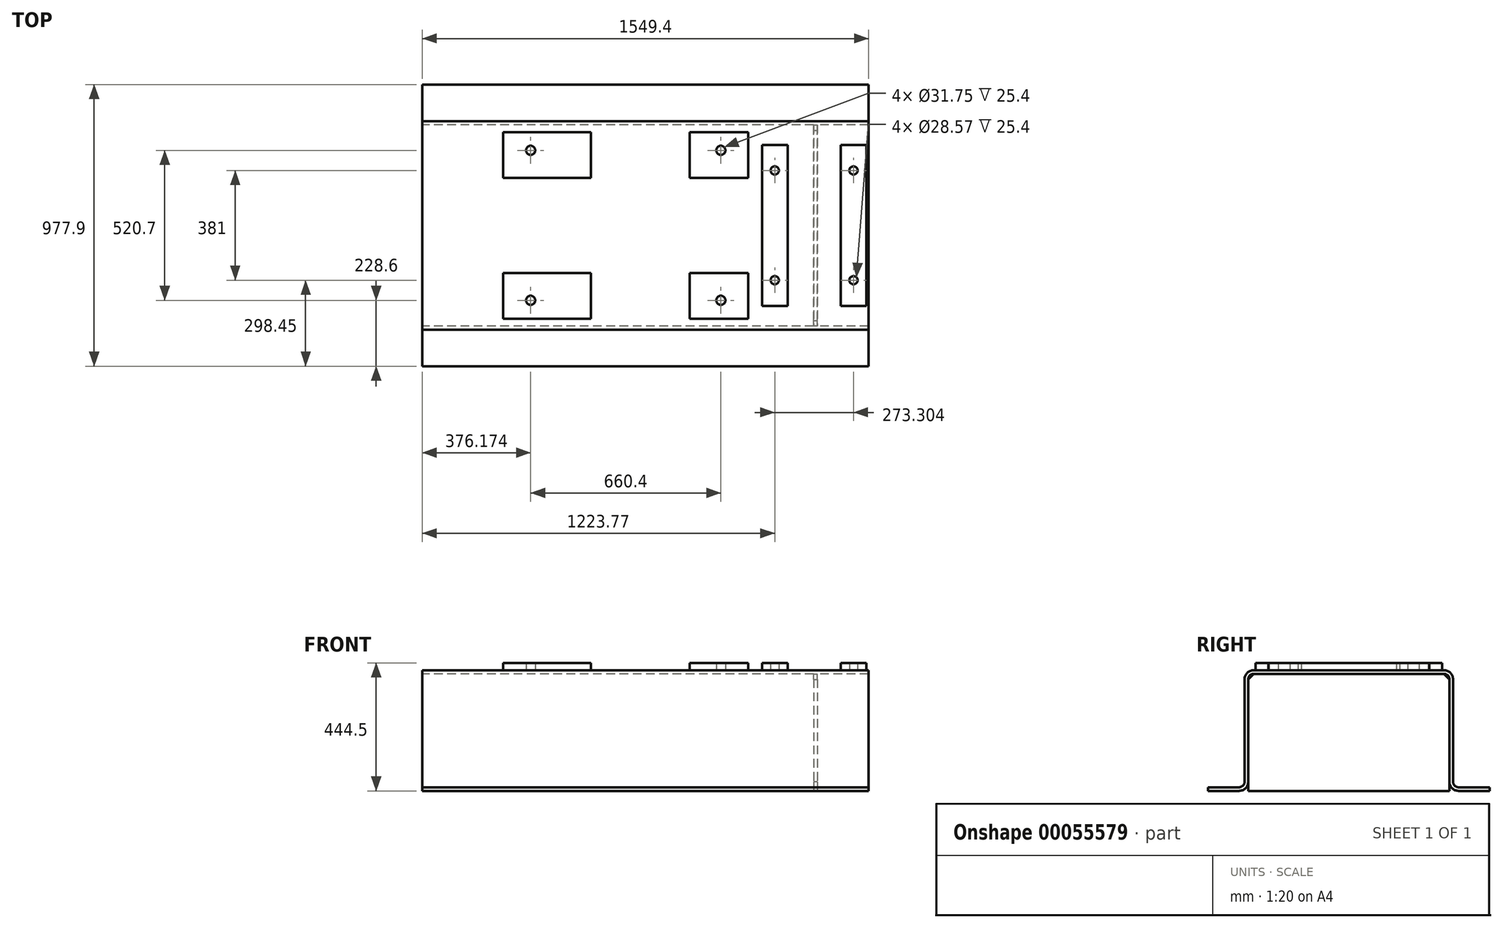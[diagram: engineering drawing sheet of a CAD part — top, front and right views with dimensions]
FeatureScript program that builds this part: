
annotation { "Feature Type Name" : "Feature", "Feature Type Description" : "" }
export const myFeature = defineFeature(function(context is Context, id is Id, definition is map)
    precondition{}
    {
        {
            var Q0;
            Q0=qCreatedBy(makeId("Right.planeOp"),FACE);
            var sketch = newSketch(context, id + "F0", { "sketchPlane" : qUnion([Q0])});
            skLineSegment(sketch, "E0.rect.bottom", {"start": v(-330.2, 209.55) * mm, "end": v(0, 209.55) * mm});
            skLineSegment(sketch, "E0.rect.top", {"start": v(-488.95, -209.55) * mm, "end": v(-381, -209.55) * mm});
            skLineSegment(sketch, "E0.rect.right", {"start": v(488.95, 209.55) * mm, "end": v(488.95, -209.55) * mm, "construction": true});
            skPoint(sketch, "E0.rect.middle", {"position": v(0, 0) * mm});
            skLineSegment(sketch, "E1", {"start": v(0, -296.04) * mm, "end": v(0, 331.56) * mm, "construction": true});
            skPoint(sketch, "E1.endSnap0", {"position": v(0, 209.55) * mm});
            skLineSegment(sketch, "E2.0", {"start": v(-361.95, 177.8) * mm, "end": v(-361.95, -177.8) * mm});
            skLineSegment(sketch, "E3.0", {"start": v(-349.25, 177.8) * mm, "end": v(-349.25, -177.8) * mm});
            skLineSegment(sketch, "E4.0", {"start": v(-488.95, -196.85) * mm, "end": v(-381, -196.85) * mm});
            skLineSegment(sketch, "E5.0", {"start": v(-330.2, 196.85) * mm, "end": v(0, 196.85) * mm});
            skLineSegment(sketch, "E6.trimOffspring", {"start": v(0, -196.85) * mm, "end": v(488.95, -196.85) * mm, "construction": true});
            skLineSegment(sketch, "E7.trimOffspring", {"start": v(0, -209.55) * mm, "end": v(488.95, -209.55) * mm, "construction": true});
            skLineSegment(sketch, "E8.trimOffspring", {"start": v(-488.95, -196.85) * mm, "end": v(-488.95, -209.55) * mm});
            skPoint(sketch, "E0.rect.left.start.orphan", {"position": v(-488.95, 209.55) * mm});
            skPoint(sketch, "E9.visualSharp", {"position": v(-349.25, 196.85) * mm});
            skArc(sketch, "E9.filletArc", {"start": v(-330.2, 196.85) * mm, "mid": v(-343.67, 191.27) * mm, "end": v(-349.25, 177.8) * mm});
            skPoint(sketch, "E10.visualSharp", {"position": v(-361.95, -196.85) * mm});
            skArc(sketch, "E10.filletArc", {"start": v(-381, -196.85) * mm, "mid": v(-367.53, -191.27) * mm, "end": v(-361.95, -177.8) * mm});
            skPoint(sketch, "E11.visualSharp", {"position": v(-349.25, -209.55) * mm});
            skArc(sketch, "E11.filletArc", {"start": v(-381, -209.55) * mm, "mid": v(-358.55, -200.25) * mm, "end": v(-349.25, -177.8) * mm});
            skPoint(sketch, "E12.visualSharp", {"position": v(-361.95, 209.55) * mm});
            skArc(sketch, "E12.filletArc", {"start": v(-330.2, 209.55) * mm, "mid": v(-352.65, 200.25) * mm, "end": v(-361.95, 177.8) * mm});
            skArc(sketch, "E13.MirrorCS", {"start": v(381, -196.85) * mm, "mid": v(367.53, -191.27) * mm, "end": v(361.95, -177.8) * mm});
            skArc(sketch, "E14.MirrorCS", {"start": v(330.2, 196.85) * mm, "mid": v(343.67, 191.27) * mm, "end": v(349.25, 177.8) * mm});
            skLineSegment(sketch, "E15.MirrorCS", {"start": v(488.95, -196.85) * mm, "end": v(488.95, -209.55) * mm});
            skArc(sketch, "E16.MirrorCS", {"start": v(330.2, 209.55) * mm, "mid": v(352.65, 200.25) * mm, "end": v(361.95, 177.8) * mm});
            skArc(sketch, "E17.MirrorCS", {"start": v(381, -209.55) * mm, "mid": v(358.55, -200.25) * mm, "end": v(349.25, -177.8) * mm});
            skLineSegment(sketch, "E18.MirrorCS", {"start": v(330.2, 209.55) * mm, "end": v(0, 209.55) * mm});
            skPoint(sketch, "E19.MirrorP", {"position": v(349.25, -209.55) * mm});
            skLineSegment(sketch, "E20.MirrorCS", {"start": v(488.95, -209.55) * mm, "end": v(381, -209.55) * mm});
            skPoint(sketch, "E21.MirrorP", {"position": v(361.95, 209.55) * mm});
            skLineSegment(sketch, "E22.MirrorCS", {"start": v(330.2, 196.85) * mm, "end": v(0, 196.85) * mm});
            skLineSegment(sketch, "E23.MirrorCS", {"start": v(488.95, -196.85) * mm, "end": v(381, -196.85) * mm});
            skPoint(sketch, "E24.MirrorP", {"position": v(488.95, 209.55) * mm});
            skPoint(sketch, "E25.MirrorP", {"position": v(361.95, -196.85) * mm});
            skLineSegment(sketch, "E26.MirrorCS", {"start": v(361.95, 177.8) * mm, "end": v(361.95, -177.8) * mm});
            skLineSegment(sketch, "E27.MirrorCS", {"start": v(349.25, 177.8) * mm, "end": v(349.25, -177.8) * mm});
            skPoint(sketch, "E28.MirrorP", {"position": v(349.25, 196.85) * mm});
            skSolve(sketch);
        }
        {
            var Q0;
            Q0=makeQuery(id+"F0.imprint","IMPRINT",FACE,{"disambiguationData":[TD([[makeQuery(id+"F0.imprint","IMPRINT",EDGE,{"derivedFrom":sQuery(id+"F0.wireOp",EDGE,"E0.rect.bottom")}),-1.0]])]});
            extrude(context, id + "F1", {"entities" : qUnion([Q0]), "endBound" : BoundingType.SYMMETRIC, "depth" : 1549.4 * mm});
        }
        {
            var Q0;
            Q0=makeQuery(id+"F1.opExtrude","SWEPT_FACE",FACE,{"disambiguationData":[OSD([sQuery(id+"F0.wireOp",EDGE,"E0.rect.bottom"),sQuery(id+"F0.wireOp",EDGE,"E18.MirrorCS")])]});
            var sketch = newSketch(context, id + "F2", { "sketchPlane" : qUnion([Q0])});
            skLineSegment(sketch, "E29.0", {"start": v(-774.7, -330.2) * mm, "end": v(-774.7, 330.2) * mm, "construction": true});
            skLineSegment(sketch, "E30.0", {"start": v(-68.33, -330.2) * mm, "end": v(-68.33, 330.2) * mm, "construction": true});
            skLineSegment(sketch, "E31.0", {"start": v(585.72, -330.2) * mm, "end": v(585.72, 330.2) * mm, "construction": true});
            skLineSegment(sketch, "E32", {"start": v(-867.52, 0) * mm, "end": v(843.8, 0) * mm, "construction": true});
            skPoint(sketch, "E32.startSnap0", {"position": v(-774.7, 0) * mm});
            skLineSegment(sketch, "E33.0", {"start": v(153.92, -330.2) * mm, "end": v(153.92, 330.2) * mm, "construction": true});
            skLineSegment(sketch, "E34.0", {"start": v(357.12, -330.2) * mm, "end": v(357.12, 330.2) * mm, "construction": true});
            skLineSegment(sketch, "E35.0", {"start": v(-188.98, -330.2) * mm, "end": v(-188.98, 330.2) * mm, "construction": true});
            skLineSegment(sketch, "E36.0", {"start": v(-493.78, -330.2) * mm, "end": v(-493.78, 330.2) * mm, "construction": true});
            skLineSegment(sketch, "E37.0", {"start": v(-867.52, -165.1) * mm, "end": v(843.8, -165.1) * mm, "construction": true});
            skLineSegment(sketch, "E38.0", {"start": v(-867.52, -323.85) * mm, "end": v(843.8, -323.85) * mm, "construction": true});
            skLineSegment(sketch, "E39.bottom", {"start": v(-188.98, -323.85) * mm, "end": v(-493.78, -323.85) * mm});
            skLineSegment(sketch, "E39.top", {"start": v(-188.98, -165.1) * mm, "end": v(-493.78, -165.1) * mm});
            skLineSegment(sketch, "E39.left", {"start": v(-188.98, -323.85) * mm, "end": v(-188.98, -165.1) * mm});
            skLineSegment(sketch, "E39.right", {"start": v(-493.78, -323.85) * mm, "end": v(-493.78, -165.1) * mm});
            skLineSegment(sketch, "E40.bottom", {"start": v(153.92, -165.1) * mm, "end": v(357.12, -165.1) * mm});
            skLineSegment(sketch, "E40.top", {"start": v(153.92, -323.85) * mm, "end": v(357.12, -323.85) * mm});
            skLineSegment(sketch, "E40.left", {"start": v(153.92, -165.1) * mm, "end": v(153.92, -323.85) * mm});
            skLineSegment(sketch, "E40.right", {"start": v(357.12, -165.1) * mm, "end": v(357.12, -323.85) * mm});
            skLineSegment(sketch, "E41.0", {"start": v(-398.53, -330.2) * mm, "end": v(-398.53, 330.2) * mm, "construction": true});
            skLineSegment(sketch, "E42.0", {"start": v(-867.52, -260.35) * mm, "end": v(843.8, -260.35) * mm, "construction": true});
            skCircle(sketch, "E43", {"center": v(-398.53, -260.35) * mm, "radius": 15.88 * mm});
            skCircle(sketch, "E44.MirrorC", {"center": v(261.87, -260.35) * mm, "radius": 15.88 * mm});
            skCircle(sketch, "E45.MirrorC", {"center": v(-398.53, 260.35) * mm, "radius": 15.88 * mm});
            skCircle(sketch, "E46.MirrorC", {"center": v(261.87, 260.35) * mm, "radius": 15.88 * mm});
            skLineSegment(sketch, "E47.MirrorCS", {"start": v(153.92, 323.85) * mm, "end": v(357.12, 323.85) * mm});
            skLineSegment(sketch, "E48.MirrorCS", {"start": v(-188.98, 323.85) * mm, "end": v(-493.78, 323.85) * mm});
            skLineSegment(sketch, "E49.MirrorCS", {"start": v(-188.98, 165.1) * mm, "end": v(-493.78, 165.1) * mm});
            skLineSegment(sketch, "E50.MirrorCS", {"start": v(-188.98, 323.85) * mm, "end": v(-188.98, 165.1) * mm});
            skLineSegment(sketch, "E51.MirrorCS", {"start": v(153.92, 165.1) * mm, "end": v(153.92, 323.85) * mm});
            skLineSegment(sketch, "E52.MirrorCS", {"start": v(357.12, 165.1) * mm, "end": v(357.12, 323.85) * mm});
            skLineSegment(sketch, "E53.MirrorCS", {"start": v(153.92, 165.1) * mm, "end": v(357.12, 165.1) * mm});
            skLineSegment(sketch, "E54.MirrorCS", {"start": v(-493.78, 323.85) * mm, "end": v(-493.78, 165.1) * mm});
            skLineSegment(sketch, "E55.0", {"start": v(493.78, -330.2) * mm, "end": v(493.78, -323.85) * mm});
            skLineSegment(sketch, "E56.0", {"start": v(404.88, -330.2) * mm, "end": v(404.88, -323.85) * mm});
            skLineSegment(sketch, "E57.trimOffspring", {"start": v(404.88, 279.4) * mm, "end": v(493.78, 279.4) * mm});
            skLineSegment(sketch, "E58.trimOffspring", {"start": v(493.78, -279.4) * mm, "end": v(493.78, 279.4) * mm});
            skLineSegment(sketch, "E59.trimOffspring", {"start": v(404.88, -279.4) * mm, "end": v(404.88, 279.4) * mm});
            skLineSegment(sketch, "E60.trimOffspring", {"start": v(404.88, -279.4) * mm, "end": v(493.78, -279.4) * mm});
            skLineSegment(sketch, "E61.0", {"start": v(449.07, -330.2) * mm, "end": v(449.07, 330.2) * mm, "construction": true});
            skLineSegment(sketch, "E62.0", {"start": v(-867.52, 190.5) * mm, "end": v(843.8, 190.5) * mm, "construction": true});
            skCircle(sketch, "E63", {"center": v(449.07, 190.5) * mm, "radius": 14.29 * mm});
            skCircle(sketch, "E64.MirrorC", {"center": v(449.07, -190.5) * mm, "radius": 14.29 * mm});
            skCircle(sketch, "E65.MirrorC", {"center": v(722.38, -190.5) * mm, "radius": 14.29 * mm});
            skCircle(sketch, "E66.MirrorC", {"center": v(722.38, 190.5) * mm, "radius": 14.29 * mm});
            skLineSegment(sketch, "E67.MirrorCS", {"start": v(766.57, -279.4) * mm, "end": v(766.57, 279.4) * mm});
            skLineSegment(sketch, "E68.MirrorCS", {"start": v(677.67, -279.4) * mm, "end": v(677.67, 279.4) * mm});
            skLineSegment(sketch, "E69.MirrorCS", {"start": v(766.57, 279.4) * mm, "end": v(677.67, 279.4) * mm});
            skLineSegment(sketch, "E70.MirrorCS", {"start": v(766.57, -279.4) * mm, "end": v(677.67, -279.4) * mm});
            skSolve(sketch);
        }
        {
            var Q0;
            Q0=qSketchRegion(id+"F2",true);
            extrude(context, id + "F3", {"entities" : qUnion([Q0]), "operationType" : NewBodyOperationType.ADD, "depth" : 25.4 * mm});
        }
        {
            var Q0;
            Q0=makeQuery(id+"F1.opExtrude","CAP_FACE",FACE,{"disambiguationData":[OSD([sQuery(id+"F0.wireOp",EDGE,"E0.rect.bottom"),sQuery(id+"F0.wireOp",EDGE,"E0.rect.top"),sQuery(id+"F0.wireOp",EDGE,"E2.0"),sQuery(id+"F0.wireOp",EDGE,"E3.0"),sQuery(id+"F0.wireOp",EDGE,"E4.0"),sQuery(id+"F0.wireOp",EDGE,"E5.0"),sQuery(id+"F0.wireOp",EDGE,"E8.trimOffspring"),sQuery(id+"F0.wireOp",EDGE,"E9.filletArc"),sQuery(id+"F0.wireOp",EDGE,"E10.filletArc"),sQuery(id+"F0.wireOp",EDGE,"E11.filletArc"),sQuery(id+"F0.wireOp",EDGE,"E12.filletArc"),sQuery(id+"F0.wireOp",EDGE,"E13.MirrorCS"),sQuery(id+"F0.wireOp",EDGE,"E14.MirrorCS"),sQuery(id+"F0.wireOp",EDGE,"E15.MirrorCS"),sQuery(id+"F0.wireOp",EDGE,"E16.MirrorCS"),sQuery(id+"F0.wireOp",EDGE,"E17.MirrorCS"),sQuery(id+"F0.wireOp",EDGE,"E18.MirrorCS"),sQuery(id+"F0.wireOp",EDGE,"E20.MirrorCS"),sQuery(id+"F0.wireOp",EDGE,"E22.MirrorCS"),sQuery(id+"F0.wireOp",EDGE,"E23.MirrorCS"),sQuery(id+"F0.wireOp",EDGE,"E26.MirrorCS"),sQuery(id+"F0.wireOp",EDGE,"E27.MirrorCS")])],"isStart":false});
            cPlane(context, id + "F4", {"entities" : qUnion([Q0]), "cplaneType" : CPlaneType.OFFSET, "offset" : 177.8 * mm, "oppositeDirection" : true, "width" : 152.4 * mm, "height" : 152.4 * mm});
        }
        {
            var Q0;
            Q0=qCreatedBy(id+"F4.planeOp",FACE);
            var sketch = newSketch(context, id + "F5", { "sketchPlane" : qUnion([Q0])});
            skLineSegment(sketch, "E71.0", {"start": v(-330.2, 196.85) * mm, "end": v(330.2, 196.85) * mm});
            skLineSegment(sketch, "E72.0", {"start": v(-349.25, 177.8) * mm, "end": v(-349.25, -209.55) * mm});
            skLineSegment(sketch, "E73.0", {"start": v(349.25, 177.8) * mm, "end": v(349.25, -209.55) * mm});
            skLineSegment(sketch, "E74.0", {"start": v(349.25, -209.55) * mm, "end": v(-349.25, -209.55) * mm});
            skPoint(sketch, "E75.orphan", {"position": v(381, -209.55) * mm});
            skPoint(sketch, "E76.orphan", {"position": v(-349.25, -177.8) * mm});
            skPoint(sketch, "E77.orphan", {"position": v(349.25, -177.8) * mm});
            skPoint(sketch, "E78.orphan", {"position": v(488.95, -209.55) * mm});
            skLineSegment(sketch, "E79", {"start": v(-349.25, 177.8) * mm, "end": v(-330.2, 196.85) * mm});
            skLineSegment(sketch, "E80", {"start": v(330.2, 196.85) * mm, "end": v(349.25, 177.8) * mm});
            skSolve(sketch);
        }
        {
            var Q0;
            Q0=qSketchRegion(id+"F5",true);
            extrude(context, id + "F6", {"entities" : qUnion([Q0]), "operationType" : NewBodyOperationType.ADD, "oppositeDirection" : true, "depth" : 12.7 * mm});
        }
    });
